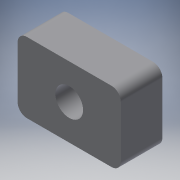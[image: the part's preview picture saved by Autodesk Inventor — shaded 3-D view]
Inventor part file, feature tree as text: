
AUTODESK INVENTOR PART (.ipt)
format: ipt  version: 2016 (Build 200138000, 138)  size: 100,864 bytes
history: native  units: in
note: dims shown in document units (in); Inventor stores cm internally (conversion verified against a paired STEP export)
features: reference x2, extrude x1, fillet x1, sketch x1
ambient origin geometry x8: Origin, YZ Plane, XZ Plane, XY Plane, X Axis, Y Axis, Z Axis, Center Point
bodies: Solid1 (feature_tree)
feature tree (5):
  extrude  "Extrusion1"  Depth=0.1772in TaperAngle=0.0deg
  fillet  "Fillet1"  Radius=0.0394in
  sketch  "Sketch1"  dims[d0=0.15in d1=0.1772in d2=0.0in d3=0.0394in]
  reference  "Reference1"
  reference  "Reference2"
